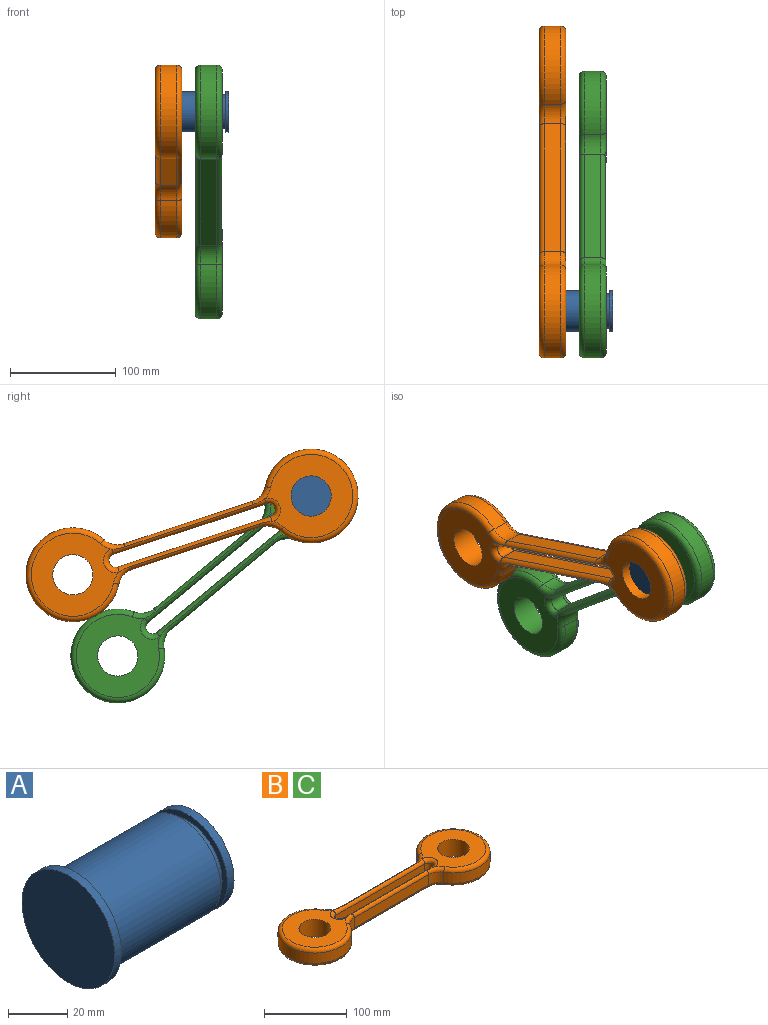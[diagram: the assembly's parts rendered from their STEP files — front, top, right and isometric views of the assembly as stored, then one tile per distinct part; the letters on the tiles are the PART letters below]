
ASSEMBLY  parts=3 mates=3
PART A: 9 faces, bbox 60.3x44.5x44.5 mm
  f0: cylinder r=19.05mm len=38.1mm, axis (-1,0,0), area 380mm2, adj f1,f8
  f1: plane 38.1x38.1mm, normal (-1,0,0), area 283.8mm2, adj f0,f2
  f2: cylinder r=16.51mm len=33.02mm, axis (-1,0,0), area 329.4mm2, adj f1,f3
  f3: plane 38.1x38.1mm, normal (1,0,0), area 283.8mm2, adj f2,f4
  f4: cylinder r=19.05mm len=50.8mm, axis (-1,0,0), area 6080.5mm2, adj f3,f5
  f5: plane 44.45x44.45mm, normal (1,0,0), area 411.7mm2, adj f4,f6
  f6: cylinder r=22.23mm len=44.45mm, axis (-1,0,0), area 443.4mm2, adj f5,f7
  f7: plane 44.45x44.45mm, normal (-1,0,0), area 1551.8mm2, adj f6
  f8: plane 38.1x38.1mm, normal (1,0,0), area 1140.1mm2, adj f0
PART B: 42 faces, bbox 333.8x96.2x25.4 mm
  f0: plane 81.37x78.74mm, normal (0,0,1), area 3632.7mm2, adj f15,f36,f39,f40,f41
  f1: plane 81.37x78.74mm, normal (0,0,-1), area 3632.7mm2, adj f15,f26,f27,f28,f29
  f2: cylinder r=19.05mm len=16.5mm, axis (0,0,-1), area 304mm2, adj f3,f13,f20,f33
  f3: cylinder r=44.45mm len=88.9mm, axis (0,0,-1), area 3547mm2, adj f2,f4,f18,f30
  f4: cylinder r=19.05mm len=16.5mm, axis (0,0,-1), area 304mm2, adj f3,f5,f19,f31
  f5: plane 127.61x15.24mm, normal (0,-1,0), area 1944.8mm2, adj f4,f6,f23,f34
  f6: cylinder r=19.05mm len=16.5mm, axis (0,0,-1), area 304mm2, adj f5,f7,f27,f39
  f7: cylinder r=44.45mm len=88.9mm, axis (0,0,-1), area 3547mm2, adj f6,f8,f29,f41
  f8: cylinder r=19.05mm len=16.5mm, axis (0,0,-1), area 304mm2, adj f7,f13,f28,f40
  f9: plane 152.4x15.24mm, normal (0,-1,0), area 2322.6mm2, adj f10,f14,f25,f37
  f10: cylinder r=6.35mm len=15.24mm, axis (0,0,-1), area 304mm2, adj f9,f11,f26,f36
  f11: plane 152.4x15.24mm, normal (0,1,0), area 2322.6mm2, adj f10,f14,f22,f35
  f12: cylinder r=19.05mm len=38.1mm, axis (0,0,-1), area 3040.2mm2, adj f16,f17
  f13: plane 127.61x15.24mm, normal (0,1,0), area 1944.8mm2, adj f2,f8,f24,f38
  f14: cylinder r=6.35mm len=15.24mm, axis (0,0,-1), area 304mm2, adj f9,f11,f21,f32
  f15: cylinder r=19.05mm len=38.1mm, axis (0,0,-1), area 3040.2mm2, adj f0,f1
  f16: plane 81.37x78.74mm, normal (0,0,1), area 3632.7mm2, adj f12,f30,f31,f32,f33
  f17: plane 81.37x78.74mm, normal (0,0,-1), area 3632.7mm2, adj f12,f18,f19,f20,f21
  f18: torus R=39.37mm, axis (0,0,1), area 1780.1mm2, adj f3,f17,f19,f20
  f19: torus R=24.13mm, axis (0,0,1), area 157.2mm2, adj f4,f17,f18,f21,f22,f23
  f20: torus R=24.13mm, axis (0,0,1), area 157.2mm2, adj f2,f17,f18,f21,f24,f25
  f21: torus R=11.43mm, axis (0,0,1), area 205.4mm2, adj f14,f17,f19,f20,f22,f25
  f22: cylinder r=5.08mm len=152.4mm, axis (-1,0,0), area 933.4mm2, adj f11,f19,f21,f23,f26,f27
  f23: cylinder r=5.08mm len=127.61mm, axis (1,0,0), area 769.1mm2, adj f5,f19,f22,f27
  f24: cylinder r=5.08mm len=127.61mm, axis (-1,0,0), area 769.1mm2, adj f13,f20,f25,f28
  f25: cylinder r=5.08mm len=152.4mm, axis (1,0,0), area 933.4mm2, adj f9,f20,f21,f24,f26,f28
  f26: torus R=11.43mm, axis (0,0,1), area 205.4mm2, adj f1,f10,f22,f25,f27,f28
  f27: torus R=24.13mm, axis (0,0,1), area 157.2mm2, adj f1,f6,f22,f23,f26,f29
  f28: torus R=24.13mm, axis (0,0,1), area 157.2mm2, adj f1,f8,f24,f25,f26,f29
  f29: torus R=39.37mm, axis (0,0,1), area 1780.1mm2, adj f1,f7,f27,f28
  f30: torus R=39.37mm, axis (0,0,1), area 1780.1mm2, adj f3,f16,f31,f33
  f31: torus R=24.13mm, axis (0,0,1), area 157.2mm2, adj f4,f16,f30,f32,f34,f35
  f32: torus R=11.43mm, axis (0,0,1), area 205.4mm2, adj f14,f16,f31,f33,f35,f37
  f33: torus R=24.13mm, axis (0,0,1), area 157.2mm2, adj f2,f16,f30,f32,f37,f38
  f34: cylinder r=5.08mm len=127.61mm, axis (-1,0,0), area 769.1mm2, adj f5,f31,f35,f39
  f35: cylinder r=5.08mm len=152.4mm, axis (1,0,0), area 933.4mm2, adj f11,f31,f32,f34,f36,f39
  f36: torus R=11.43mm, axis (0,0,1), area 205.4mm2, adj f0,f10,f35,f37,f39,f40
  f37: cylinder r=5.08mm len=152.4mm, axis (-1,0,0), area 933.4mm2, adj f9,f32,f33,f36,f38,f40
  f38: cylinder r=5.08mm len=127.61mm, axis (1,0,0), area 769.1mm2, adj f13,f33,f37,f40
  f39: torus R=24.13mm, axis (0,0,1), area 157.2mm2, adj f0,f6,f34,f35,f36,f41
  f40: torus R=24.13mm, axis (0,0,1), area 157.2mm2, adj f0,f8,f36,f37,f38,f41
  f41: torus R=39.37mm, axis (0,0,1), area 1780.1mm2, adj f0,f7,f39,f40
PART C: same geometry as B
PLACE A t=(-29.77,-13.62,5.36)mm fixed
PLACE B rot(axis=(-0.63,-0.46,0.63),131.1deg) t=(-73.86,99.18,-31.91)mm
PLACE C rot(axis=(-0.67,-0.32,0.67),145deg) t=(-35.76,77.92,-70.37)mm
MATE parallel B.f12 <-> C.f17  axis (1,0,0) through (-73.86,-13.62,5.36)mm
MATE revolute C.f12 <-> A.f0  axis (1,0,0) through (-61.16,-13.62,5.36)mm
MATE revolute B.f12 <-> A.f0  axis (1,0,0) through (-86.56,-13.62,5.36)mm
